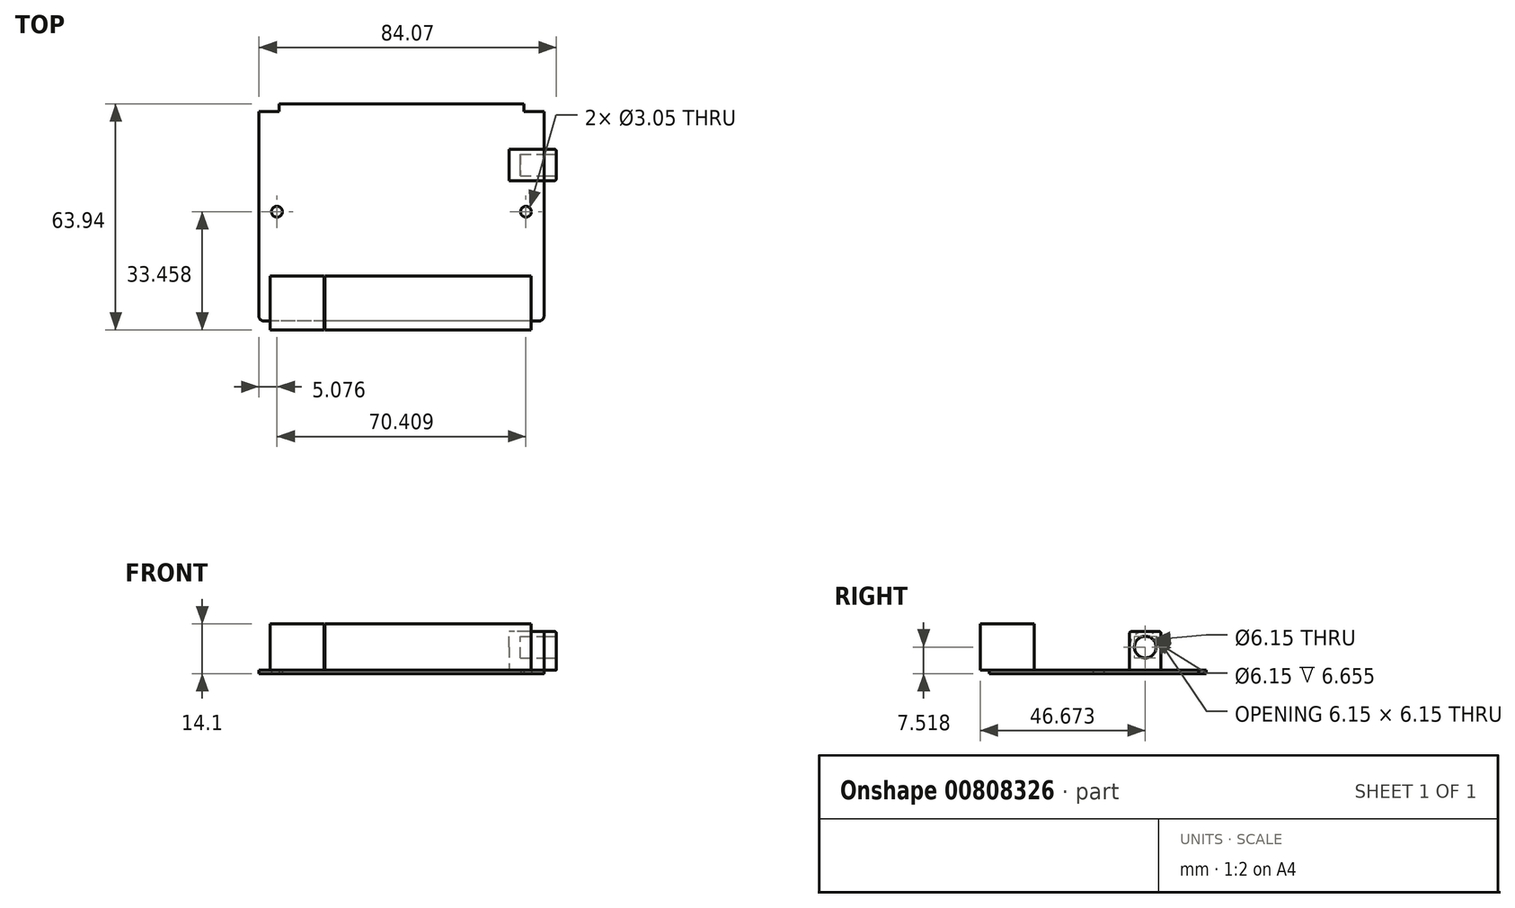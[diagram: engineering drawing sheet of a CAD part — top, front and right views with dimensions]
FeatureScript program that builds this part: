
annotation { "Feature Type Name" : "Feature", "Feature Type Description" : "" }
export const myFeature = defineFeature(function(context is Context, id is Id, definition is map)
    precondition{}
    {
        {
            var Q0;
            Q0=qCreatedBy(makeId("Top.planeOp"),FACE);
            var sketch = newSketch(context, id + "F0", { "sketchPlane" : qUnion([Q0])});
            skLineSegment(sketch, "E0.bottom", {"start": v(39.01, -30.66) * mm, "end": v(-39.01, -30.66) * mm});
            skLineSegment(sketch, "E0.top", {"start": v(34.57, 30.66) * mm, "end": v(-34.57, 30.66) * mm});
            skLineSegment(sketch, "E0.left", {"start": v(40.28, -29.39) * mm, "end": v(40.28, 28.5) * mm});
            skLineSegment(sketch, "E0.right", {"start": v(-40.28, -29.39) * mm, "end": v(-40.28, 28.5) * mm});
            skPoint(sketch, "E0.middle", {"position": v(0, 0) * mm});
            skLineSegment(sketch, "E1", {"start": v(40.28, 28.5) * mm, "end": v(-40.28, 28.5) * mm, "construction": true});
            skLineSegment(sketch, "E2", {"start": v(40.28, 28.5) * mm, "end": v(34.57, 28.5) * mm, "construction": true});
            skLineSegment(sketch, "E3", {"start": v(-40.28, 28.5) * mm, "end": v(-34.57, 28.5) * mm, "construction": true});
            skLineSegment(sketch, "E4", {"start": v(-40.28, 28.5) * mm, "end": v(-34.57, 28.5) * mm});
            skLineSegment(sketch, "E5", {"start": v(-34.57, 28.5) * mm, "end": v(-34.57, 30.66) * mm});
            skLineSegment(sketch, "E6", {"start": v(40.28, 28.5) * mm, "end": v(34.57, 28.5) * mm});
            skLineSegment(sketch, "E7", {"start": v(34.57, 28.5) * mm, "end": v(34.57, 30.66) * mm});
            skPoint(sketch, "E8.orphan", {"position": v(40.28, 30.66) * mm});
            skPoint(sketch, "E9.orphan", {"position": v(-40.28, 30.66) * mm});
            skPoint(sketch, "E10.visualSharp", {"position": v(-40.28, -30.66) * mm});
            skArc(sketch, "E10.filletArc", {"start": v(-40.28, -29.39) * mm, "mid": v(-39.91, -30.29) * mm, "end": v(-39.01, -30.66) * mm});
            skPoint(sketch, "E11.visualSharp", {"position": v(40.28, -30.66) * mm});
            skArc(sketch, "E11.filletArc", {"start": v(39.01, -30.66) * mm, "mid": v(39.91, -30.29) * mm, "end": v(40.28, -29.39) * mm});
            skLineSegment(sketch, "E12", {"start": v(-40.28, 28.5) * mm, "end": v(-40.28, 0.18) * mm, "construction": true});
            skLineSegment(sketch, "E13", {"start": v(-40.28, 0.18) * mm, "end": v(40.28, 0.18) * mm, "construction": true});
            skLineSegment(sketch, "E14", {"start": v(-40.28, 0.18) * mm, "end": v(-35.2, 0.18) * mm, "construction": true});
            skLineSegment(sketch, "E15", {"start": v(40.28, 0.18) * mm, "end": v(35.2, 0.18) * mm, "construction": true});
            skCircle(sketch, "E16", {"center": v(-35.2, 0.18) * mm, "radius": 1.52 * mm});
            skCircle(sketch, "E17", {"center": v(35.2, 0.18) * mm, "radius": 1.52 * mm});
            skLineSegment(sketch, "E18", {"start": v(34.57, 28.5) * mm, "end": v(34.57, 13.26) * mm, "construction": true});
            skLineSegment(sketch, "E19", {"start": v(34.57, 13.26) * mm, "end": v(40.28, 13.26) * mm, "construction": true});
            skSolve(sketch);
        }
        {
            var Q0;
            Q0 = qSketchRegion(id + "F0", true);
            extrude(context, id + "F1", {"entities" : qUnion([Q0]), "depth" : 1.02 * mm, "offsetDistance" : 25.4 * mm});
        }
        {
            var Q0;
            Q0=makeQuery(id+"F1.opExtrude","CAP_FACE",FACE,{"disambiguationData":[OSD([sQuery(id+"F0.wireOp",EDGE,"E0.bottom"),sQuery(id+"F0.wireOp",EDGE,"E0.top"),sQuery(id+"F0.wireOp",EDGE,"E0.left"),sQuery(id+"F0.wireOp",EDGE,"E0.right"),sQuery(id+"F0.wireOp",EDGE,"E4"),sQuery(id+"F0.wireOp",EDGE,"E5"),sQuery(id+"F0.wireOp",EDGE,"E6"),sQuery(id+"F0.wireOp",EDGE,"E7"),sQuery(id+"F0.wireOp",EDGE,"E10.filletArc"),sQuery(id+"F0.wireOp",EDGE,"E11.filletArc"),sQuery(id+"F0.wireOp",EDGE,"E16"),sQuery(id+"F0.wireOp",EDGE,"E17")])],"isStart":false});
            var sketch = newSketch(context, id + "F2", { "sketchPlane" : qUnion([Q0])});
            skLineSegment(sketch, "E20.bottom", {"start": v(43.79, 8.92) * mm, "end": v(40.28, 8.92) * mm});
            skLineSegment(sketch, "E20.top", {"start": v(43.79, 17.86) * mm, "end": v(40.28, 17.86) * mm});
            skLineSegment(sketch, "E20.left", {"start": v(43.79, 8.92) * mm, "end": v(43.79, 17.86) * mm});
            skLineSegment(sketch, "E20.right", {"start": v(40.28, 8.92) * mm, "end": v(40.28, 17.86) * mm});
            skPoint(sketch, "E20.middle", {"position": v(42.04, 13.4) * mm});
            skLineSegment(sketch, "E21.bottom", {"start": v(40.28, 17.86) * mm, "end": v(30.38, 17.86) * mm});
            skLineSegment(sketch, "E21.top", {"start": v(40.28, 8.92) * mm, "end": v(30.38, 8.92) * mm});
            skLineSegment(sketch, "E21.left", {"start": v(40.28, 17.86) * mm, "end": v(40.28, 8.92) * mm});
            skLineSegment(sketch, "E21.right", {"start": v(30.38, 17.86) * mm, "end": v(30.38, 8.92) * mm});
            skSolve(sketch);
        }
        {
            var Q0;
            Q0=makeQuery(id+"F2.imprint","IMPRINT",FACE,{"disambiguationData":[TD([[makeQuery(id+"F2.imprint","IMPRINT",EDGE,{"derivedFrom":sQuery(id+"F2.wireOp",EDGE,"E20.bottom")}),-1.0]])]});
            extrude(context, id + "F3", {"entities" : qUnion([Q0]), "depth" : 10.95 * mm, "offsetDistance" : 25.4 * mm});
        }
        {
            var Q0;
            Q0=makeQuery(id+"F2.imprint","IMPRINT",FACE,{"disambiguationData":[TD([[makeQuery(id+"F2.imprint","IMPRINT",EDGE,{"derivedFrom":sQuery(id+"F2.wireOp",EDGE,"E21.bottom")}),1.0]])]});
            extrude(context, id + "F4", {"entities" : qUnion([Q0]), "depth" : 10.95 * mm, "offsetDistance" : 25.4 * mm});
        }
        {
            var Q0;
            Q0=makeQuery(id+"F4.opExtrude","CAP_EDGE",EDGE,{"disambiguationData":[OSD([sQuery(id+"F2.wireOp",EDGE,"E21.top")])],"isStart":false});
            var Q1;
            Q1=makeQuery(id+"F4.opExtrude","CAP_EDGE",EDGE,{"disambiguationData":[OSD([sQuery(id+"F2.wireOp",EDGE,"E21.bottom")])],"isStart":false});
            fillet(context, id + "F5", {"entities" : qUnion([Q0, Q1]), "radius" : 4.44 * mm, "tangentPropagation" : true, "allowEdgeOverflow" : false});
        }
        {
            var Q0;
            Q0=makeQuery(id+"F3.opExtrude","CAP_EDGE",EDGE,{"disambiguationData":[OSD([sQuery(id+"F2.wireOp",EDGE,"E20.bottom")])],"isStart":false});
            var Q1;
            Q1=makeQuery(id+"F3.opExtrude","CAP_EDGE",EDGE,{"disambiguationData":[OSD([sQuery(id+"F2.wireOp",EDGE,"E20.left")])],"isStart":false});
            var Q2;
            Q2=makeQuery(id+"F3.opExtrude","CAP_EDGE",EDGE,{"disambiguationData":[OSD([sQuery(id+"F2.wireOp",EDGE,"E20.top")])],"isStart":false});
            var Q3;
            Q3=makeQuery(id+"F3.opExtrude","SWEPT_EDGE",EDGE,{"disambiguationData":[OSD([sQuery(id+"F2.wireOp",EDGE,"E20.bottom"),sQuery(id+"F2.wireOp",EDGE,"E20.left")])]});
            var Q4;
            Q4=makeQuery(id+"F3.opExtrude","SWEPT_EDGE",EDGE,{"disambiguationData":[OSD([sQuery(id+"F2.wireOp",EDGE,"E20.top"),sQuery(id+"F2.wireOp",EDGE,"E20.left")])]});
            fillet(context, id + "F6", {"entities" : qUnion([Q0, Q1, Q2, Q3, Q4]), "radius" : 0.64 * mm, "tangentPropagation" : true, "allowEdgeOverflow" : false});
        }
        {
            var Q0;
            Q0=makeQuery(id+"F3.opExtrude","SWEPT_FACE",FACE,{"disambiguationData":[OSD([sQuery(id+"F2.wireOp",EDGE,"E20.left")])]});
            var sketch = newSketch(context, id + "F7", { "sketchPlane" : qUnion([Q0])});
            skCircle(sketch, "E22", {"center": v(13.4, 7.52) * mm, "radius": 3.07 * mm});
            skPoint(sketch, "E22.centerSnap0", {"position": v(13.4, 11.33) * mm});
            skSolve(sketch);
        }
        {
            var Q0;
            Q0=makeQuery(id+"F7.imprint","IMPRINT",FACE,{"disambiguationData":[TD([[makeQuery(id+"F7.imprint","IMPRINT",EDGE,{"derivedFrom":sQuery(id+"F7.wireOp",EDGE,"E22")}),1.0]])]});
            extrude(context, id + "F8", {"entities" : qUnion([Q0]), "operationType" : NewBodyOperationType.REMOVE, "oppositeDirection" : true, "depth" : 10.16 * mm, "offsetDistance" : 25.4 * mm});
        }
        {
            var Q0;
            {var subQ1=sQuery(id+"F2.wireOp",EDGE,"E21.bottom");Q0=makeQuery(id+"F2.imprint","IMPRINT",FACE,{"disambiguationData":[TD([[makeQuery(id+"F2.imprint","IMPRINT",EDGE,{"derivedFrom":subQ1}),-1.0]])]});}
            var sketch = newSketch(context, id + "F9", { "sketchPlane" : qUnion([Q0])});
            skLineSegment(sketch, "E23", {"start": v(0, -30.68) * mm, "end": v(0, -17.98) * mm, "construction": true});
            skLineSegment(sketch, "E24", {"start": v(40.28, -17.98) * mm, "end": v(36.6, -17.98) * mm, "construction": true});
            skLineSegment(sketch, "E25", {"start": v(36.6, -17.98) * mm, "end": v(36.6, -30.66) * mm, "construction": true});
            skLineSegment(sketch, "E26", {"start": v(36.6, -17.98) * mm, "end": v(-21.7, -17.98) * mm, "construction": true});
            skLineSegment(sketch, "E27.bottom", {"start": v(-21.7, -17.98) * mm, "end": v(36.6, -17.98) * mm});
            skLineSegment(sketch, "E27.top", {"start": v(-21.7, -33.28) * mm, "end": v(36.6, -33.28) * mm});
            skLineSegment(sketch, "E27.left", {"start": v(-21.7, -17.98) * mm, "end": v(-21.7, -33.28) * mm});
            skLineSegment(sketch, "E27.right", {"start": v(36.6, -17.98) * mm, "end": v(36.6, -33.28) * mm});
            skSolve(sketch);
        }
        {
            var Q0;
            Q0 = qSketchRegion(id + "F9", true);
            extrude(context, id + "F10", {"entities" : qUnion([Q0]), "operationType" : NewBodyOperationType.ADD, "depth" : 13.08 * mm, "offsetDistance" : 25.4 * mm});
        }
        {
            var Q0;
            {var subQ1=sQuery(id+"F2.wireOp",EDGE,"E21.bottom");Q0=makeQuery(id+"F2.imprint","IMPRINT",FACE,{"disambiguationData":[TD([[makeQuery(id+"F2.imprint","IMPRINT",EDGE,{"derivedFrom":subQ1}),-1.0]])]});}
            var sketch = newSketch(context, id + "F11", { "sketchPlane" : qUnion([Q0])});
            skLineSegment(sketch, "E28", {"start": v(-21.87, -17.98) * mm, "end": v(-21.87, -30.66) * mm, "construction": true});
            skLineSegment(sketch, "E29.bottom", {"start": v(-21.87, -17.98) * mm, "end": v(-37.1, -17.98) * mm});
            skLineSegment(sketch, "E29.top", {"start": v(-21.87, -33.28) * mm, "end": v(-37.1, -33.28) * mm});
            skLineSegment(sketch, "E29.left", {"start": v(-21.87, -17.98) * mm, "end": v(-21.87, -33.28) * mm});
            skLineSegment(sketch, "E29.right", {"start": v(-37.1, -17.98) * mm, "end": v(-37.1, -33.28) * mm});
            skSolve(sketch);
        }
        {
            var Q0;
            Q0 = qSketchRegion(id + "F11", true);
            extrude(context, id + "F12", {"entities" : qUnion([Q0]), "operationType" : NewBodyOperationType.ADD, "depth" : 13.08 * mm, "offsetDistance" : 25.4 * mm});
        }
    });
